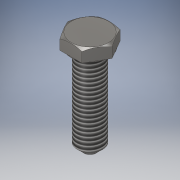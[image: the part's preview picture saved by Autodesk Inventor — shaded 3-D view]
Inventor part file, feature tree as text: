
AUTODESK INVENTOR PART (.ipt)
format: ipt  version: 2018 (Build 220112000, 112)  size: 153,088 bytes
history: native  units: in
note: dims shown in document units (in); Inventor stores cm internally (conversion verified against a paired STEP export)
features: sketch x3, revolve x2, extrude x2, chamfer x1, thread x1, projected_geometry x1
ambient origin geometry x8: Origin, YZ Plane, XZ Plane, XY Plane, X Axis, Y Axis, Z Axis, Center Point
bodies: Solid1 (feature_tree)
feature tree (10):
  revolve  "Revolution1"  [1 undecoded]
  chamfer  "Chamfer1"  Distance=0.125in Angle=45.0deg
  extrude  "Extrusion1"  Depth=0.25in TaperAngle=0.0deg
  extrude  "Extrusion2"  Depth=0.235in TaperAngle=0.0deg
  revolve  "Revolution2"  Angle=30.0deg
  thread  "Thread3"  [1 undecoded]
  sketch  "Sketch1"  dims[d0=0.5in d1=1.75in]
  sketch  "Sketch2"  dims[d2=90.0deg d3=0.125in d4=0.125in d5=45.0deg]
  sketch  "Sketch3"  dims[d6=0.75in d7=0.25in d8=0.0in d9=0.235in d10=0.0in d11=30.0deg d12=90.0deg d17=0.04in d21=1.0in d22=0.0in]
  projected_geometry  "Projected Loop1"
note: 2 required parameter values undecoded (feature->parameter linkage not recoverable at this tier; creation-order binding heuristic only, values carry confidence <= 0.55)